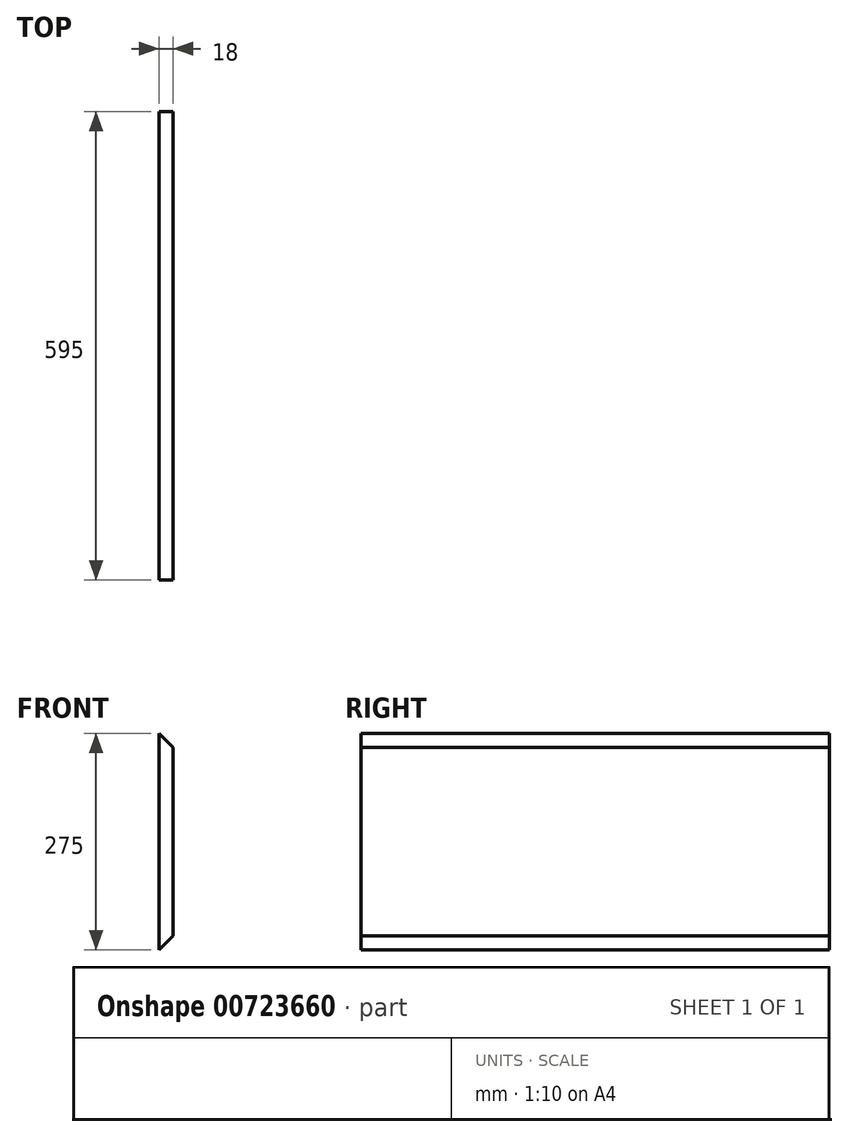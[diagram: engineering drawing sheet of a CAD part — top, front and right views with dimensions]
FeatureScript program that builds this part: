
annotation { "Feature Type Name" : "Feature", "Feature Type Description" : "" }
export const myFeature = defineFeature(function(context is Context, id is Id, definition is map)
    precondition{}
    {
        {
            var Q0;
            Q0=qCreatedBy(makeId("Right.planeOp"),FACE);
            var sketch = newSketch(context, id + "F0", { "sketchPlane" : qUnion([Q0])});
            skLineSegment(sketch, "E0.bottom", {"start": v(-297.5, 137.5) * mm, "end": v(297.5, 137.5) * mm});
            skLineSegment(sketch, "E0.top", {"start": v(-297.5, -137.5) * mm, "end": v(297.5, -137.5) * mm});
            skLineSegment(sketch, "E0.left", {"start": v(-297.5, 137.5) * mm, "end": v(-297.5, -137.5) * mm});
            skLineSegment(sketch, "E0.right", {"start": v(297.5, 137.5) * mm, "end": v(297.5, -137.5) * mm});
            skLineSegment(sketch, "E1", {"start": v(-297.5, 137.5) * mm, "end": v(297.5, -137.5) * mm, "construction": true});
            skLineSegment(sketch, "E2", {"start": v(297.5, 137.5) * mm, "end": v(-297.5, -137.5) * mm, "construction": true});
            skSolve(sketch);
        }
        {
            var Q0;
            Q0 = qSketchRegion(id + "F0", true);
            extrude(context, id + "F1", {"entities" : qUnion([Q0]), "depth" : 18 * mm, "offsetDistance" : 25 * mm});
        }
        {
            var Q0;
            Q0=makeQuery(id+"F1.opExtrude","CAP_EDGE",EDGE,{"disambiguationData":[OSD([sQuery(id+"F0.wireOp",EDGE,"E0.bottom")])],"isStart":false});
            var Q1;
            Q1=makeQuery(id+"F1.opExtrude","CAP_EDGE",EDGE,{"disambiguationData":[OSD([sQuery(id+"F0.wireOp",EDGE,"E0.top")])],"isStart":false});
            chamfer(context, id + "F2", {"entities" : qUnion([Q0, Q1]), "width" : 18 * mm, "tangentPropagation" : true});
        }
    });
